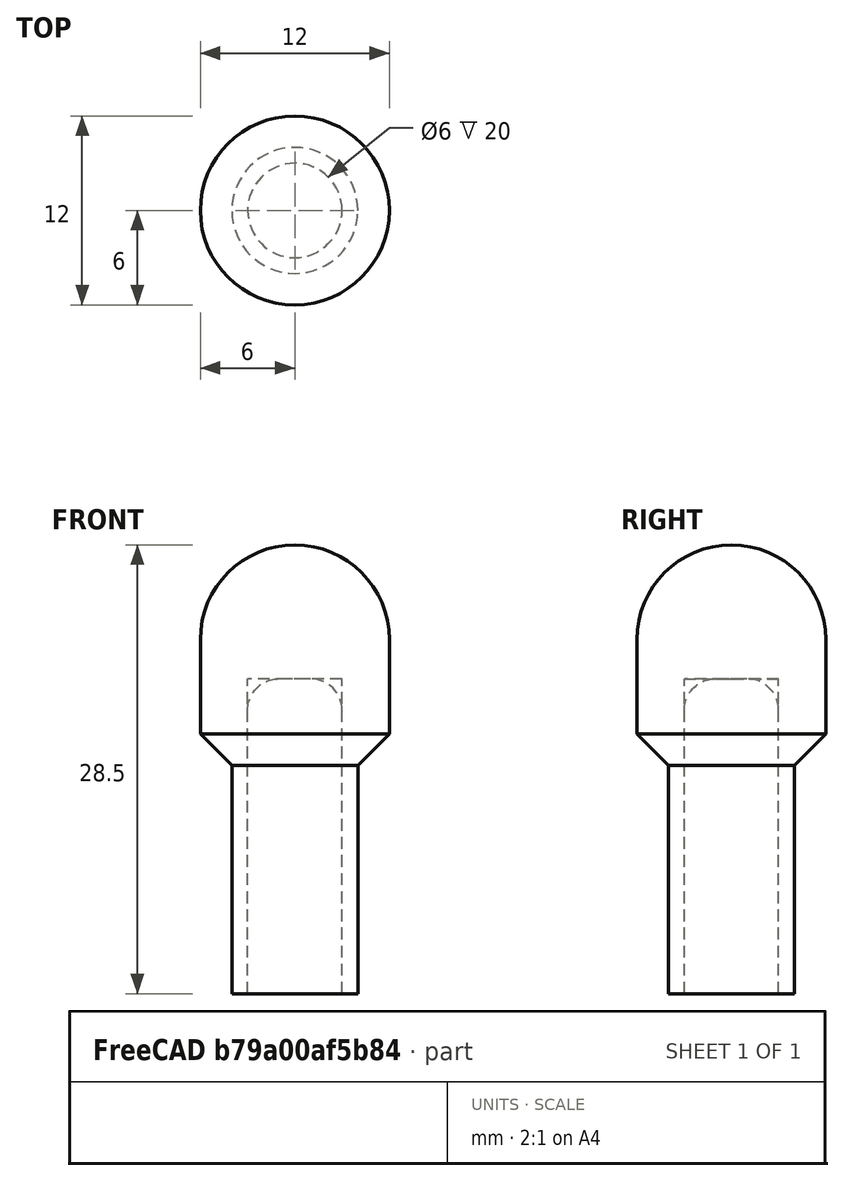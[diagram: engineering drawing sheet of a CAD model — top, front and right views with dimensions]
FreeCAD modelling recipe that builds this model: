
FCSTD DOCUMENT  (FreeCAD 0.18R4 (GitTag))
Label: AHCP Switch Top
License: All rights reserved
LicenseURL: http://en.wikipedia.org/wiki/All_rights_reserved
objects: Part::Cylinder×4, Part::Sphere×1, Part::Cone×1, Part::MultiFuse×1, Part::Cut×1, Part::Fillet×1
note: 9 computed .brp shape members not serialized (recipe doc carries the construction recipe); baked Part::Feature solids carry a one-line shape summary decoded from their .brp

FEATURE [Part::Sphere] Sphere
  Angle1 = -90
  Angle2 = 90
  Angle3 = 360
  AttacherType = Attacher::AttachEngine3D
  Placement = pos=(0,0,22.5) rot=(0,0,1;0rad)
  Radius = 6
FEATURE [Part::Cylinder] Cylinder002
  Angle = 360
  AttacherType = Attacher::AttachEngine3D
  Height = 6
  Placement = pos=(0,0,16.5) rot=(0,0,1;0rad)
  Radius = 6
FEATURE [Part::Cylinder] Cylinder
  Angle = 360
  AttacherType = Attacher::AttachEngine3D
  Height = 20
  Radius = 3
FEATURE [Part::Cone] Cone
  Angle = 360
  AttacherType = Attacher::AttachEngine3D
  Height = 2
  Placement = pos=(0,0,14.5) rot=(0,0,1;0rad)
  Radius1 = 4
  Radius2 = 6
FEATURE [Part::Cylinder] Cylinder003
  Angle = 360
  AttacherType = Attacher::AttachEngine3D
  Height = 15
  Radius = 4
FEATURE [Part::MultiFuse] Fusion
  Shapes = -> [Cylinder003,Cone,Cylinder002,Sphere]
FEATURE [Part::Cut] Cut
  Base = -> Fusion
  Tool = -> Cylinder
FEATURE [Part::Cylinder] Cylinder005
  Angle = 360
  AttacherType = Attacher::AttachEngine3D
  Height = 20
  Radius = 3
FEATURE [Part::Fillet] Fillet001
  Base = -> Cylinder005
  Edges = 1 edges r=2: [Edge1]
